# Revit family: АНТАРЕС_Воздушная завеса_1203A_Ed_ESd_ELd+++
name_source: partatom
category: Оборудование
units: mm (PartAtom-declared; Revit-internal decimal feet)

## family parameters
Всегда вертикально = Да
Классификация = Нет
На основе рабочей плоскости = Нет
Общий = Нет
При загрузке вырезать с полостями = Нет
Размер круглого соединителя = Использовать диаметр
Тип детали = Нормальный
Точка расчета площади = Нет

## types (4) — shared parameters
ADSK_URL документации изделия = https://antar.ru
ADSK_Единица измерения = шт.
ADSK_Завод-изготовитель = ООО ''АНТАРЕС ПРО''
ADSK_Количество = 1
ADSK_Материал = АНТАРЕС_Белый
ADSK_Напряжение = 380 В
ADSK_Размер_Высота = 305 мм
ADSK_Размер_Глубина = 397 мм
ADSK_Размер_Ширина = 1170 мм
URL = https://antar.ru
Воздухопроизводительность = 4760.0 м³/ч
Регулировка угла выдува воздушной струи (град.) = 0...+30
Тип установки (горизонтальный / вертикальный) = Универсальный

## per-type parameters (varying)
| type | ADSK_Масса | ADSK_Наименование | ADSK_Номинальная мощность | Степень защиты | Уровень шума дБ(А) |
| 1203A | 40 | Завеса воздушная "АНТАРЕС" серия Универсал-ПРО" модель 1203 А | 750 Вт | IP54 | 71 |
| 1203Ed | 42 | Завеса воздушная "АНТАРЕС" серия "Универсал-ПРО" модель 1203 Еd | 12750 Вт | IP20 | 52/71 |
| 1203ESd | 42 | Завеса воздушная "АНТАРЕС" серия "Универсал-ПРО" модель 1203 ЕSd | 18750 Вт | IP20 | 52/71 |
| 1203ELd | 42 | Завеса воздушная "АНТАРЕС" серия "Универсал-ПРО" модель 1203 ЕLd | 24750 Вт | IP20 | 52/71 |

note: column(s) folded — value = type name in every type: ADSK_Марка
